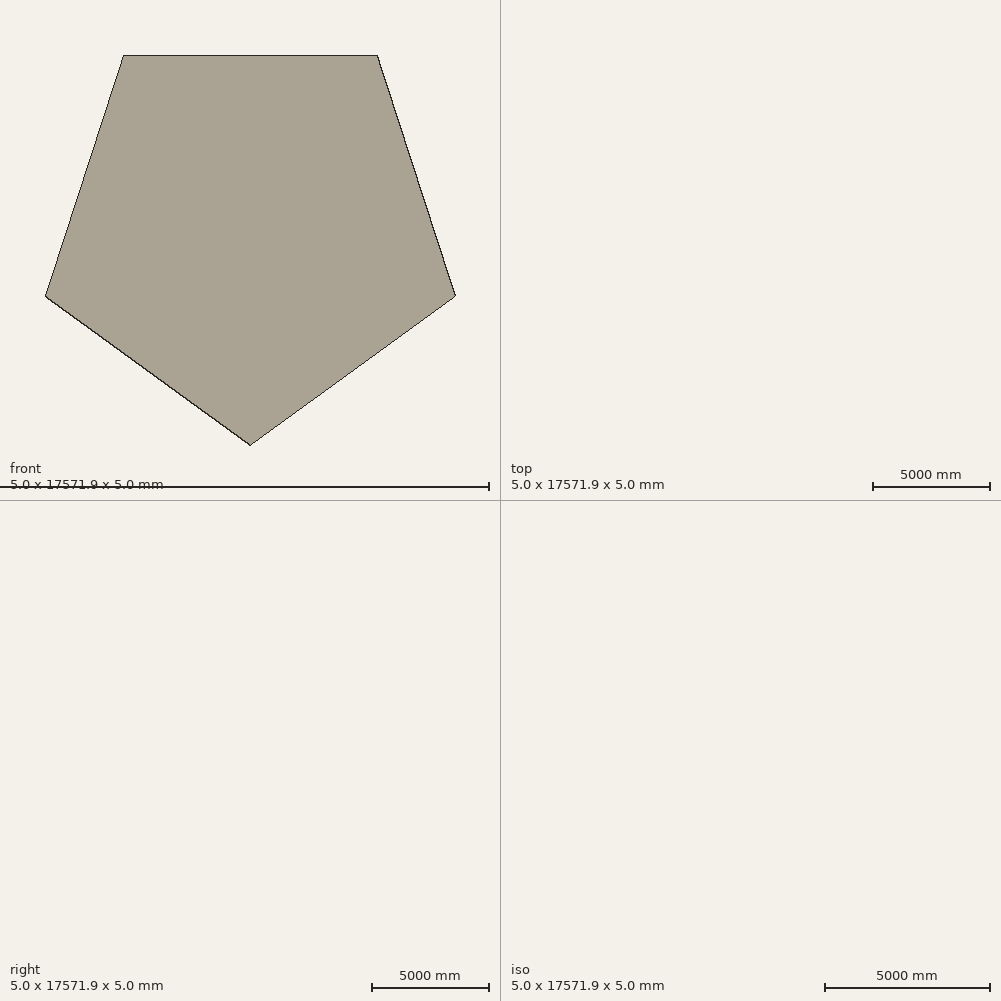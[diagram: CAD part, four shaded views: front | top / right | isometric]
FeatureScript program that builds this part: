
annotation { "Feature Type Name" : "Feature", "Feature Type Description" : "" }
export const myFeature = defineFeature(function(context is Context, id is Id, definition is map)
    precondition{}
    {
        {
            var Q0;
            Q0=qCreatedBy(makeId("Front.planeOp"),FACE);
            var sketch = newSketch(context, id + "F0", { "sketchPlane" : qUnion([Q0])});
            skCircle(sketch, "E0", {"center": v(0, 0) * mm, "radius": 2.5 * mm});
            skSolve(sketch);
        }
        {
            var Q0;
            Q0=qSketchRegion(id+"F0",true);
            extrude(context, id + "F1", {"entities" : qUnion([Q0]), "depth" : 17571.92 * mm, "offsetDistance" : 25 * mm});
        }
    });
